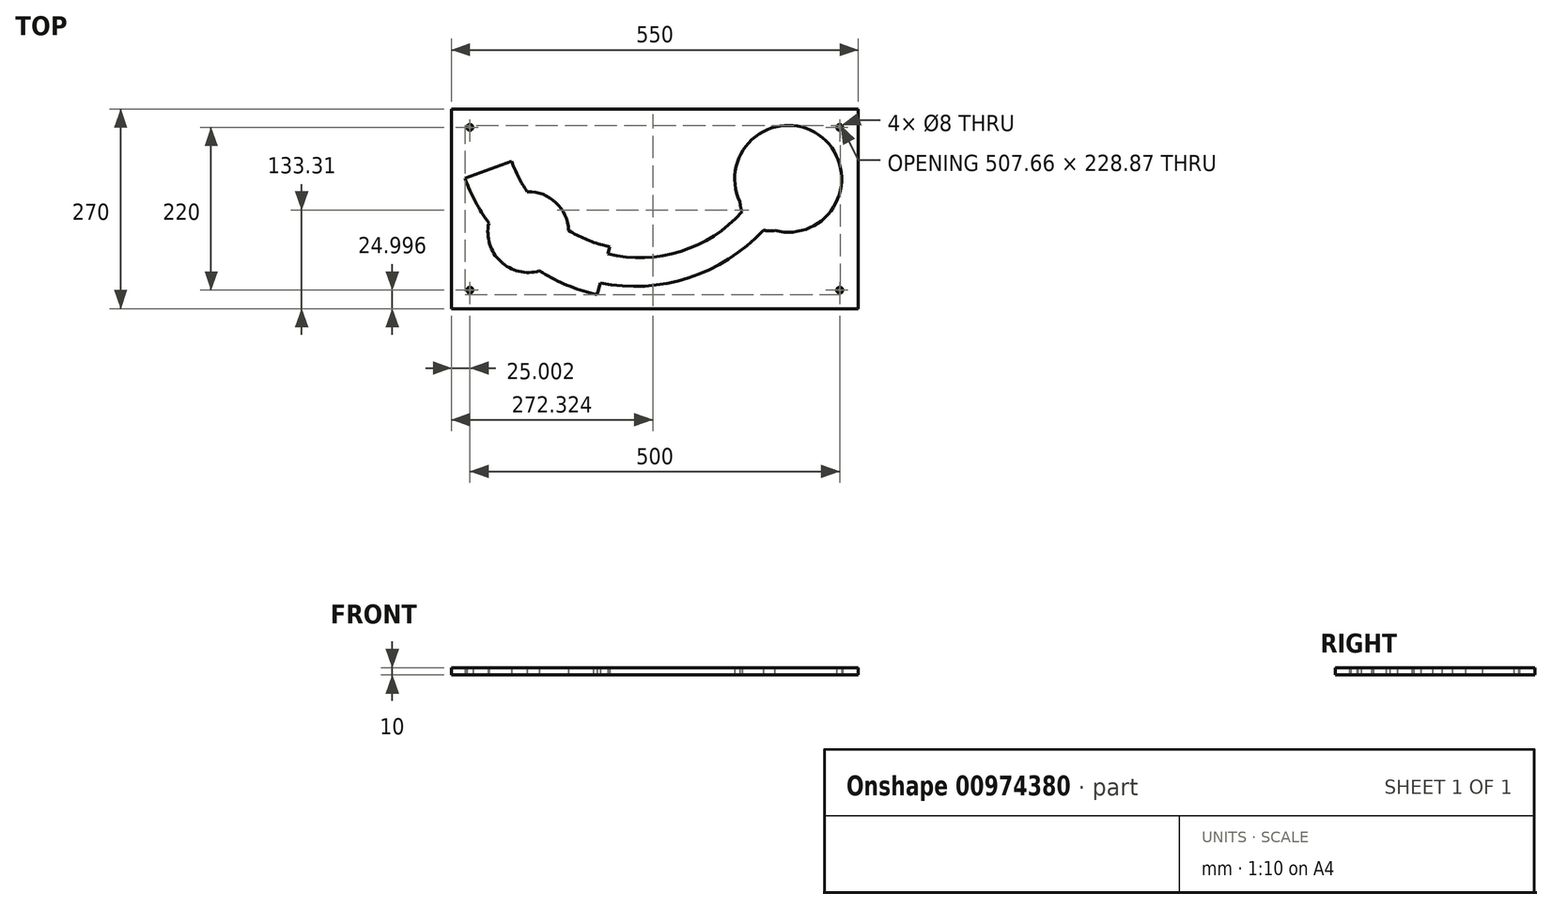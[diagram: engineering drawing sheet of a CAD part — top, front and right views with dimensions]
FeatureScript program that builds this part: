
annotation { "Feature Type Name" : "Feature", "Feature Type Description" : "" }
export const myFeature = defineFeature(function(context is Context, id is Id, definition is map)
    precondition{}
    {
        {
            var Q0;
            Q0=qCreatedBy(makeId("Top.planeOp"),FACE);
            var sketch = newSketch(context, id + "F0", { "sketchPlane" : qUnion([Q0])});
            skArc(sketch, "E0", {"start": v(-230.92, 0) * mm, "mid": v(-216.97, -31.4) * mm, "end": v(-198.82, -60.58) * mm});
            skArc(sketch, "E1", {"start": v(-167.95, 22.88) * mm, "mid": v(-158.73, 1.8) * mm, "end": v(-146.92, -17.92) * mm});
            skLineSegment(sketch, "E2", {"start": v(-167.95, 22.88) * mm, "end": v(-230.92, 0) * mm});
            skLineSegment(sketch, "E3.bottom", {"start": v(-249.4, 93.94) * mm, "end": v(300.6, 93.94) * mm});
            skLineSegment(sketch, "E3.top", {"start": v(-249.4, -176.06) * mm, "end": v(300.6, -176.06) * mm});
            skLineSegment(sketch, "E3.left", {"start": v(-249.4, 93.94) * mm, "end": v(-249.4, -176.06) * mm});
            skLineSegment(sketch, "E3.right", {"start": v(300.6, 93.94) * mm, "end": v(300.6, -176.06) * mm});
            skArc(sketch, "E4", {"start": v(187.63, -70.45) * mm, "mid": v(252.02, 55.12) * mm, "end": v(140.78, -31.7) * mm});
            skPoint(sketch, "E4.third.point", {"position": v(271.17, -31.7) * mm});
            skArc(sketch, "E5", {"start": v(-91, -70.48) * mm, "mid": v(-108.17, -32.72) * mm, "end": v(-146.92, -17.92) * mm});
            skArc(sketch, "E6.trimOffspring", {"start": v(-91, -70.48) * mm, "mid": v(-68.53, -81.92) * mm, "end": v(-44.68, -90.13) * mm});
            skArc(sketch, "E7.trimOffspring", {"start": v(-130.35, -124.92) * mm, "mid": v(-118.29, -132.08) * mm, "end": v(-105.83, -138.55) * mm});
            skLineSegment(sketch, "E8.bottom", {"start": v(300.6, 93.94) * mm, "end": v(275.6, 93.94) * mm});
            skLineSegment(sketch, "E8.left", {"start": v(300.6, 93.94) * mm, "end": v(300.6, 68.94) * mm});
            skLineSegment(sketch, "E9.bottom", {"start": v(300.6, -176.06) * mm, "end": v(275.6, -176.06) * mm});
            skLineSegment(sketch, "E9.left", {"start": v(300.6, -176.06) * mm, "end": v(300.6, -151.06) * mm});
            skCircle(sketch, "E10", {"center": v(275.6, 68.94) * mm, "radius": 4 * mm});
            skCircle(sketch, "E11", {"center": v(275.6, -151.06) * mm, "radius": 4 * mm});
            skLineSegment(sketch, "E12.bottom", {"start": v(-249.4, 93.94) * mm, "end": v(-224.4, 93.94) * mm});
            skLineSegment(sketch, "E12.left", {"start": v(-249.4, 93.94) * mm, "end": v(-249.4, 68.94) * mm});
            skCircle(sketch, "E13", {"center": v(-224.4, 68.94) * mm, "radius": 4 * mm});
            skCircle(sketch, "E14", {"center": v(-224.4, -151.06) * mm, "radius": 4 * mm});
            skArc(sketch, "E15", {"start": v(140.78, -31.7) * mm, "mid": v(141.59, -38.46) * mm, "end": v(143.52, -45) * mm});
            skArc(sketch, "E16", {"start": v(-38.07, -102.23) * mm, "mid": v(60.63, -98.7) * mm, "end": v(143.52, -45) * mm});
            skArc(sketch, "E17", {"start": v(-48.37, -141.3) * mm, "mid": v(71.27, -134.34) * mm, "end": v(172.3, -69.89) * mm});
            skArc(sketch, "E18.trimOffspring", {"start": v(172.3, -69.89) * mm, "mid": v(179.94, -70.9) * mm, "end": v(187.63, -70.45) * mm});
            skArc(sketch, "E19.trimOffspring", {"start": v(-198.82, -60.58) * mm, "mid": v(-182.94, -112.27) * mm, "end": v(-130.35, -124.92) * mm});
            skArc(sketch, "E20.trimOffspring", {"start": v(-79.46, -149.48) * mm, "mid": v(-70.8, -152.32) * mm, "end": v(-62.02, -154.85) * mm});
            skArc(sketch, "E21", {"start": v(-130.35, -124.92) * mm, "mid": v(-105.6, -138.65) * mm, "end": v(-79.46, -149.48) * mm});
            skLineSegment(sketch, "E22", {"start": v(-44.68, -90.13) * mm, "end": v(-40.68, -91.2) * mm});
            skLineSegment(sketch, "E23", {"start": v(-62.02, -154.85) * mm, "end": v(-57.67, -156.01) * mm});
            skPoint(sketch, "E24.orphan", {"position": v(-60.36, -166.27) * mm});
            skPoint(sketch, "E25.end.orphan", {"position": v(-60.36, -148.88) * mm});
            skLineSegment(sketch, "E26", {"start": v(-57.67, -156.01) * mm, "end": v(-52.56, -157.19) * mm});
            skLineSegment(sketch, "E27", {"start": v(-52.56, -157.19) * mm, "end": v(-35.52, -92.56) * mm});
            skLineSegment(sketch, "E28", {"start": v(-40.68, -91.2) * mm, "end": v(-35.52, -92.56) * mm});
            skSolve(sketch);
        }
        {
            var Q0;
            Q0=makeQuery(id+"F0.imprint","IMPRINT",FACE,{"disambiguationData":[TD([[makeQuery(id+"F0.imprint","IMPRINT",EDGE,{"derivedFrom":sQuery(id+"F0.wireOp",EDGE,"E0")}),-1.0]])]});
            extrude(context, id + "F1", {"entities" : qUnion([Q0]), "depth" : 10 * mm, "offsetDistance" : 25 * mm});
        }
    });
